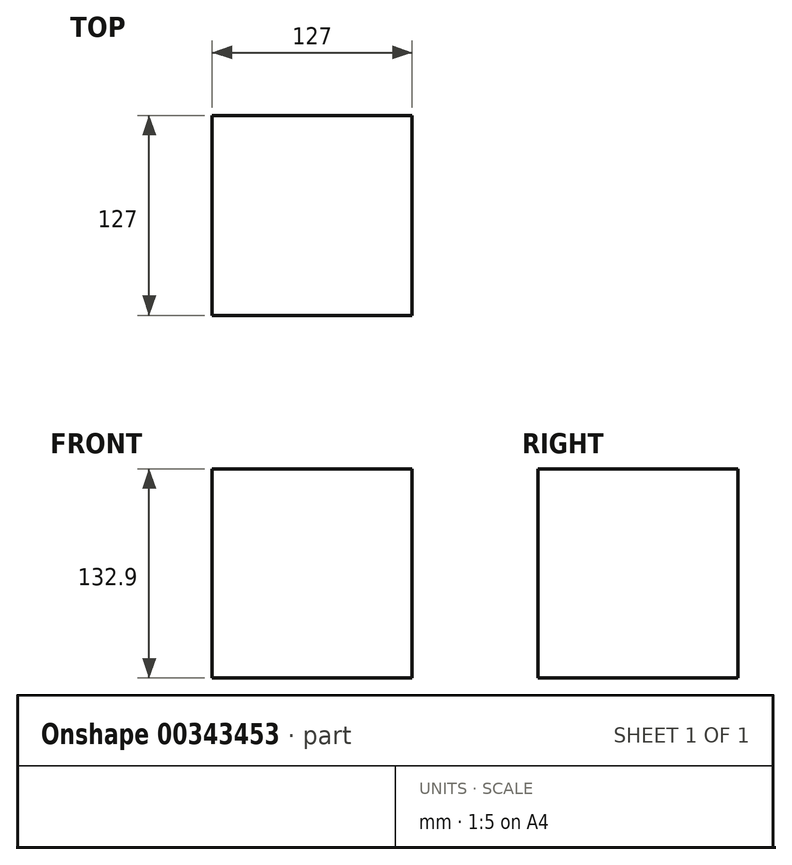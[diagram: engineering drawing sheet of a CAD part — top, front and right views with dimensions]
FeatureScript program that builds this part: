
annotation { "Feature Type Name" : "Feature", "Feature Type Description" : "" }
export const myFeature = defineFeature(function(context is Context, id is Id, definition is map)
    precondition{}
    {
        {
            var Q0;
            Q0=qCreatedBy(makeId("Front.planeOp"),FACE);
            var sketch = newSketch(context, id + "F0", { "sketchPlane" : qUnion([Q0])});
            skLineSegment(sketch, "E0.bottom", {"start": v(-111.16, 98.25) * mm, "end": v(15.84, 98.25) * mm});
            skLineSegment(sketch, "E0.top", {"start": v(-111.16, -34.65) * mm, "end": v(15.84, -34.65) * mm});
            skLineSegment(sketch, "E0.left", {"start": v(-111.16, 98.25) * mm, "end": v(-111.16, -34.65) * mm});
            skLineSegment(sketch, "E0.right", {"start": v(15.84, 98.25) * mm, "end": v(15.84, -34.65) * mm});
            skSolve(sketch);
        }
        {
            var Q0;
            Q0=makeQuery(id+"F0.imprint","IMPRINT",FACE,{"disambiguationData":[TD([[makeQuery(id+"F0.imprint","IMPRINT",EDGE,{"derivedFrom":sQuery(id+"F0.wireOp",EDGE,"E0.bottom")}),-1.0]])]});
            extrude(context, id + "F1", {"entities" : qUnion([Q0]), "depth" : 127 * mm});
        }
    });
